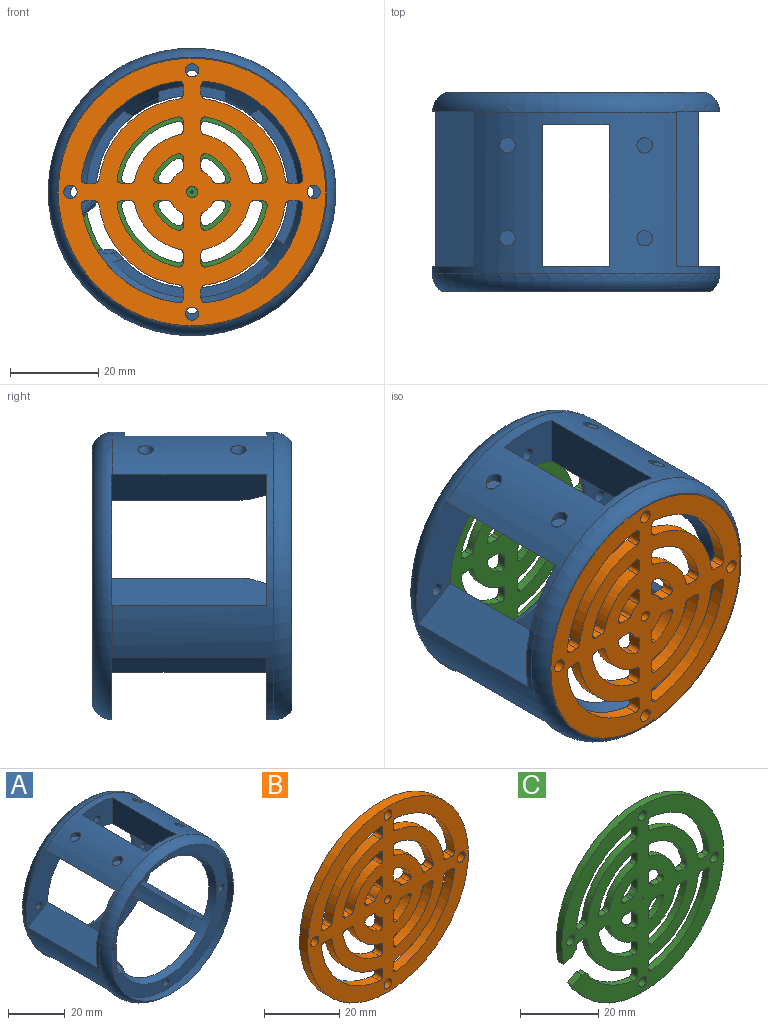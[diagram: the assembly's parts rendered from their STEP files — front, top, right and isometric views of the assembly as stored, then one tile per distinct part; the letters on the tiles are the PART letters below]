
ASSEMBLY  parts=3 mates=1
PART A: 57 faces, bbox 70.6x46.6x70.6 mm
  f0: torus R=28.75mm, axis (0,-1,0), area 6.5mm2, adj f9,f21,f33,f54
  f1: torus R=28.75mm, axis (0,-1,0), area 15.9mm2, adj f9,f21,f50,f55
  f2: cylinder r=1.5mm len=3mm, axis (0,1,0), area 22.1mm2, adj f13,f49
  f3: cylinder r=1.5mm len=3mm, axis (0,1,0), area 22.1mm2, adj f13,f53
  f4: cylinder r=1.5mm len=3mm, axis (0,1,0), area 22.1mm2, adj f13,f45
  f5: torus R=28.75mm, axis (0,-1,0), area 23mm2, adj f9,f21,f43,f47
  f6: cylinder r=1.5mm len=3mm, axis (0,-1,0), area 25mm2, adj f8,f42
  f7: torus R=28.75mm, axis (0,-1,0), area 21.7mm2, adj f9,f21,f44,f51
  f8: plane 61.12x61.12mm, normal (0,-1,0), area 883mm2, adj f6,f11,f16,f17,f18,f20,f21,f32
  f9: cylinder r=21.75mm len=43.5mm, axis (0,1,0), area 709.7mm2, adj f0,f1,f5,f7,f30,f34,f36,f38
  f10: cylinder r=32.5mm len=65mm, axis (0,1,0), area 2231.8mm2, adj f14,f15,f22,f24,f26,f28,f41,f42
  f11: cylinder r=30.5mm len=61mm, axis (0,-1,0), area 574.9mm2, adj f8,f15
  f12: cylinder r=29.5mm len=59mm, axis (0,1,0), area 370.7mm2, adj f13,f14
  f13: plane 59x59mm, normal (0,1,0), area 879.8mm2, adj f2,f3,f4,f12,f19,f31,f36
  f14: torus R=27.5mm, axis (0,1,0), area 1114mm2, adj f10,f12,f45,f47,f48,f49,f50,f51
  f15: torus R=27.5mm, axis (0,-1,0), area 926.8mm2, adj f10,f11
  f16: cylinder r=1.5mm len=3mm, axis (0,-1,0), area 25mm2, adj f8,f56
  f17: cylinder r=1.5mm len=3mm, axis (0,-1,0), area 25mm2, adj f8,f46
  f18: cylinder r=1.5mm len=3mm, axis (0,-1,0), area 25mm2, adj f8,f52
  f19: cylinder r=1.5mm len=5.35mm, axis (0,1,0), area 50.4mm2, adj f13,f41
  f20: cylinder r=5mm len=38mm, axis (0,1,0), area 517.1mm2, adj f8,f31,f32,f33,f34,f38,f39,f40
  f21: cone r=25.25mm half-angle=26.6deg, axis (0,-1,0), area 507.2mm2, adj f0,f1,f5,f7,f8,f30,f32,f40
  f22: cylinder r=1.75mm len=3.5mm, axis (0,0,1), area 11.3mm2, adj f10,f23
  f23: plane 3.5x3.5mm, normal (0,0,1), area 9.6mm2, adj f22
  f24: cylinder r=1.75mm len=3.5mm, axis (0,0,1), area 11.3mm2, adj f10,f25
  f25: plane 3.5x3.5mm, normal (0,0,1), area 9.6mm2, adj f24
  f26: cylinder r=1.75mm len=3.5mm, axis (0,0,1), area 11.3mm2, adj f10,f27
  f27: plane 3.5x3.5mm, normal (0,0,1), area 9.6mm2, adj f26
  f28: cylinder r=1.75mm len=3.5mm, axis (0,0,1), area 11.3mm2, adj f10,f29
  f29: plane 3.5x3.5mm, normal (0,0,1), area 9.6mm2, adj f28
  f30: torus R=28.75mm, axis (0,-1,0), area 4.3mm2, adj f9,f21,f39,f48
  f31: torus R=7mm, axis (0,1,0), area 51.5mm2, adj f13,f20,f35,f37
  f32: bspline ~10.87x6.72mm, area 12.7mm2, adj f8,f20,f21,f33
  f33: bspline ~5.68x2.87mm, area 6.4mm2, adj f0,f20,f32,f34
  f34: cylinder r=2mm len=29.35mm, axis (0,1,0), area 66.7mm2, adj f9,f20,f33,f35
  f35: sphere r=2mm, area 4.9mm2, adj f31,f34,f36
  f36: torus R=23.75mm, axis (0,1,0), area 401.8mm2, adj f9,f13,f35,f37
  f37: sphere r=2mm, area 4.9mm2, adj f31,f36,f38
  f38: cylinder r=2mm len=29.35mm, axis (0,1,0), area 66.7mm2, adj f9,f20,f37,f39
  f39: bspline ~5.68x2.38mm, area 6.4mm2, adj f20,f30,f38,f40
  f40: bspline ~10.87x5.31mm, area 12.7mm2, adj f8,f20,f21,f39
  f41: plane 15x12.08mm, normal (0,-1,0), area 156.4mm2, adj f9,f10,f19,f43,f44
  f42: plane 15x9.78mm, normal (0,1,0), area 123.2mm2, adj f6,f10,f21,f43,f44
  f43: plane 32.13x11.34mm, normal (1,0,0), area 353.4mm2, adj f5,f9,f10,f21,f41,f42
  f44: plane 32.13x11.34mm, normal (-1,0,0), area 353.4mm2, adj f7,f9,f10,f21,f41,f42
  f45: plane 29.47x19.13mm, normal (0,-1,0), area 273.9mm2, adj f4,f9,f14,f47,f48
  f46: plane 29.48x17.13mm, normal (0,1,0), area 227.4mm2, adj f10,f17,f21,f47,f48
  f47: plane 35.14x9.85mm, normal (-0.51,0,-0.86), area 389.3mm2, adj f5,f9,f10,f14,f21,f45,f46
  f48: plane 35.2x10.28mm, normal (-0.52,0,0.85), area 407.3mm2, adj f9,f10,f14,f21,f30,f45,f46
  f49: plane 40.21x19.44mm, normal (0,-1,0), area 395.8mm2, adj f2,f9,f14,f50,f51
  f50: plane 35.04x8.8mm, normal (0.58,0,0.81), area 372.9mm2, adj f1,f9,f10,f14,f21,f49,f52
  f51: plane 35.14x9.76mm, normal (0.52,0,-0.85), area 389.5mm2, adj f7,f9,f10,f14,f21,f49,f52
  f52: plane 40.22x17.46mm, normal (0,1,0), area 325.4mm2, adj f10,f18,f21,f50,f51
  f53: plane 50.92x17.92mm, normal (0,-1,0), area 499.6mm2, adj f3,f9,f14,f54,f55
  f54: plane 35.18x11.39mm, normal (0.28,0,-0.96), area 402.7mm2, adj f0,f9,f10,f14,f21,f53,f56
  f55: plane 35.01x8mm, normal (-0.67,0,-0.74), area 371.3mm2, adj f1,f9,f10,f14,f21,f53,f56
  f56: plane 50.93x16.66mm, normal (0,1,0), area 417.4mm2, adj f10,f16,f21,f54,f55
PART B: 104 faces, bbox 60.5x3x60.5 mm
  f0: plane 3x2.2mm, normal (0,0,-1), area 6.6mm2, adj f50,f51,f93,f102
  f1: cylinder r=9.25mm len=5.25mm, axis (0,1,0), area 22.9mm2, adj f50,f51,f93,f94
  f2: plane 3x2.2mm, normal (1,0,0), area 6.6mm2, adj f50,f51,f94,f103
  f3: cylinder r=9.25mm len=5.25mm, axis (0,1,0), area 22.9mm2, adj f50,f51,f90,f91
  f4: plane 3x2.2mm, normal (0,0,-1), area 6.6mm2, adj f50,f51,f91,f100
  f5: cylinder r=5.25mm len=3mm, axis (0,1,0), area 9mm2, adj f50,f51,f100,f101
  f6: plane 3x2.04mm, normal (0,0,-1), area 6.1mm2, adj f50,f51,f85,f92
  f7: cylinder r=17.25mm len=13.77mm, axis (0,1,0), area 62.1mm2, adj f50,f51,f85,f87
  f8: plane 3x2.04mm, normal (1,0,0), area 6.1mm2, adj f50,f51,f87,f95
  f9: cylinder r=9.25mm len=5.25mm, axis (0,1,0), area 22.9mm2, adj f50,f51,f78,f81
  f10: plane 3x2.2mm, normal (-1,0,0), area 6.6mm2, adj f50,f51,f78,f98
  f11: cylinder r=5.25mm len=3mm, axis (0,1,0), area 9mm2, adj f50,f51,f98,f99
  f12: plane 3x2.2mm, normal (1,0,0), area 6.6mm2, adj f50,f51,f79,f97
  f13: cylinder r=9.25mm len=5.25mm, axis (0,1,0), area 22.9mm2, adj f50,f51,f79,f82
  f14: plane 3x2.2mm, normal (0,0,1), area 6.6mm2, adj f50,f51,f82,f96
  f15: plane 3x2.04mm, normal (-1,0,0), area 6.1mm2, adj f50,f51,f72,f89
  f16: cylinder r=17.25mm len=13.77mm, axis (0,1,0), area 62.1mm2, adj f50,f51,f72,f73
  f17: plane 3x2.04mm, normal (0,0,-1), area 6.1mm2, adj f50,f51,f73,f88
  f18: cylinder r=17.25mm len=13.77mm, axis (0,1,0), area 62.1mm2, adj f50,f51,f70,f71
  f19: plane 3x2.04mm, normal (0,0,1), area 6.1mm2, adj f50,f51,f71,f83
  f20: cylinder r=13.25mm len=10.16mm, axis (0,1,0), area 45.6mm2, adj f50,f51,f76,f83
  f21: plane 3x2.04mm, normal (0,0,1), area 6.1mm2, adj f50,f51,f65,f80
  f22: cylinder r=17.25mm len=13.77mm, axis (0,1,0), area 62.1mm2, adj f50,f51,f65,f66
  f23: plane 3x2.04mm, normal (-1,0,0), area 6.1mm2, adj f50,f51,f66,f77
  f24: plane 3x2.02mm, normal (-1,0,0), area 6.1mm2, adj f50,f51,f62,f75
  f25: cylinder r=25.25mm len=21.93mm, axis (0,1,0), area 100.2mm2, adj f50,f51,f62,f63
  f26: plane 3x2.02mm, normal (0,0,-1), area 6.1mm2, adj f50,f51,f63,f74
  f27: plane 3x2.02mm, normal (0,0,-1), area 6.1mm2, adj f50,f51,f60,f84
  f28: cylinder r=25.25mm len=21.93mm, axis (0,1,0), area 100.2mm2, adj f50,f51,f60,f61
  f29: plane 3x2.02mm, normal (1,0,0), area 6.1mm2, adj f50,f51,f61,f86
  f30: plane 3x2.02mm, normal (1,0,0), area 6.1mm2, adj f50,f51,f58,f69
  f31: cylinder r=25.25mm len=21.93mm, axis (0,1,0), area 100.2mm2, adj f50,f51,f58,f59
  f32: plane 3x2.02mm, normal (0,0,1), area 6.1mm2, adj f50,f51,f59,f68
  f33: cylinder r=25.25mm len=21.93mm, axis (0,1,0), area 100.2mm2, adj f50,f51,f56,f57
  f34: plane 3x2.02mm, normal (-1,0,0), area 6.1mm2, adj f50,f51,f57,f67
  f35: cylinder r=21.25mm len=18.19mm, axis (0,1,0), area 82.9mm2, adj f50,f51,f64,f67
  f36: cylinder r=5.25mm len=3mm, axis (0,1,0), area 9mm2, adj f50,f51,f102,f103
  f37: plane 3x2.2mm, normal (-1,0,0), area 6.6mm2, adj f50,f51,f90,f101
  f38: cylinder r=13.25mm len=10.16mm, axis (0,1,0), area 45.6mm2, adj f50,f51,f92,f95
  f39: plane 3x2.2mm, normal (0,0,1), area 6.6mm2, adj f50,f51,f81,f99
  f40: cylinder r=5.25mm len=3mm, axis (0,1,0), area 9mm2, adj f50,f51,f96,f97
  f41: cylinder r=13.25mm len=10.16mm, axis (0,1,0), area 45.6mm2, adj f50,f51,f88,f89
  f42: plane 3x2.04mm, normal (1,0,0), area 6.1mm2, adj f50,f51,f70,f76
  f43: cylinder r=13.25mm len=10.16mm, axis (0,1,0), area 45.6mm2, adj f50,f51,f77,f80
  f44: cylinder r=21.25mm len=18.19mm, axis (0,1,0), area 82.9mm2, adj f50,f51,f74,f75
  f45: cylinder r=21.25mm len=18.19mm, axis (0,1,0), area 82.9mm2, adj f50,f51,f84,f86
  f46: cylinder r=21.25mm len=18.19mm, axis (0,1,0), area 82.9mm2, adj f50,f51,f68,f69
  f47: plane 3x2.02mm, normal (0,0,1), area 6.1mm2, adj f50,f51,f56,f64
  f48: cylinder r=30.25mm len=60.5mm, axis (0,1,0), area 570.2mm2, adj f50,f51
  f49: cylinder r=1.25mm len=3mm, axis (0,1,0), area 23.6mm2, adj f50,f51
  f50: plane 60.5x60.5mm, normal (0,-1,0), area 1896mm2, adj f0,f1,f2,f3,f4,f5,f6,f7
  f51: plane 60.5x60.5mm, normal (0,1,0), area 1896mm2, adj f0,f1,f2,f3,f4,f5,f6,f7
  f52: cylinder r=1.5mm len=3mm, axis (0,-1,0), area 28.3mm2, adj f50,f51
  f53: cylinder r=1.5mm len=3mm, axis (0,-1,0), area 28.3mm2, adj f50,f51
  f54: cylinder r=1.5mm len=3mm, axis (0,-1,0), area 28.3mm2, adj f50,f51
  f55: cylinder r=1.5mm len=3mm, axis (0,-1,0), area 28.3mm2, adj f50,f51
  f56: cylinder r=1mm len=3mm, axis (0,1,0), area 5.1mm2, adj f33,f47,f50,f51
  f57: cylinder r=1mm len=3mm, axis (0,1,0), area 5.1mm2, adj f33,f34,f50,f51
  f58: cylinder r=1mm len=3mm, axis (0,1,0), area 5.1mm2, adj f30,f31,f50,f51
  f59: cylinder r=1mm len=3mm, axis (0,1,0), area 5.1mm2, adj f31,f32,f50,f51
  f60: cylinder r=1mm len=3mm, axis (0,1,0), area 5.1mm2, adj f27,f28,f50,f51
  f61: cylinder r=1mm len=3mm, axis (0,1,0), area 5.1mm2, adj f28,f29,f50,f51
  f62: cylinder r=1mm len=3mm, axis (0,1,0), area 5.1mm2, adj f24,f25,f50,f51
  f63: cylinder r=1mm len=3mm, axis (0,1,0), area 5.1mm2, adj f25,f26,f50,f51
  f64: cylinder r=1mm len=3mm, axis (0,1,0), area 4.3mm2, adj f35,f47,f50,f51
  f65: cylinder r=1mm len=3mm, axis (0,1,0), area 5.3mm2, adj f21,f22,f50,f51
  f66: cylinder r=1mm len=3mm, axis (0,1,0), area 5.3mm2, adj f22,f23,f50,f51
  f67: cylinder r=1mm len=3mm, axis (0,1,0), area 4.3mm2, adj f34,f35,f50,f51
  f68: cylinder r=1mm len=3mm, axis (0,1,0), area 4.3mm2, adj f32,f46,f50,f51
  f69: cylinder r=1mm len=3mm, axis (0,1,0), area 4.3mm2, adj f30,f46,f50,f51
  f70: cylinder r=1mm len=3mm, axis (0,1,0), area 5.3mm2, adj f18,f42,f50,f51
  f71: cylinder r=1mm len=3mm, axis (0,1,0), area 5.3mm2, adj f18,f19,f50,f51
  f72: cylinder r=1mm len=3mm, axis (0,1,0), area 5.3mm2, adj f15,f16,f50,f51
  f73: cylinder r=1mm len=3mm, axis (0,1,0), area 5.3mm2, adj f16,f17,f50,f51
  f74: cylinder r=1mm len=3mm, axis (0,1,0), area 4.3mm2, adj f26,f44,f50,f51
  f75: cylinder r=1mm len=3mm, axis (0,1,0), area 4.3mm2, adj f24,f44,f50,f51
  f76: cylinder r=1mm len=3mm, axis (0,1,0), area 4.1mm2, adj f20,f42,f50,f51
  f77: cylinder r=1mm len=3mm, axis (0,1,0), area 4.1mm2, adj f23,f43,f50,f51
  f78: cylinder r=1mm len=3mm, axis (0,1,0), area 5.8mm2, adj f9,f10,f50,f51
  f79: cylinder r=1mm len=3mm, axis (0,1,0), area 5.8mm2, adj f12,f13,f50,f51
  f80: cylinder r=1mm len=3mm, axis (0,1,0), area 4.1mm2, adj f21,f43,f50,f51
  f81: cylinder r=1mm len=3mm, axis (0,1,0), area 5.8mm2, adj f9,f39,f50,f51
  f82: cylinder r=1mm len=3mm, axis (0,1,0), area 5.8mm2, adj f13,f14,f50,f51
  f83: cylinder r=1mm len=3mm, axis (0,1,0), area 4.1mm2, adj f19,f20,f50,f51
  f84: cylinder r=1mm len=3mm, axis (0,1,0), area 4.3mm2, adj f27,f45,f50,f51
  f85: cylinder r=1mm len=3mm, axis (0,1,0), area 5.3mm2, adj f6,f7,f50,f51
  f86: cylinder r=1mm len=3mm, axis (0,1,0), area 4.3mm2, adj f29,f45,f50,f51
  f87: cylinder r=1mm len=3mm, axis (0,1,0), area 5.3mm2, adj f7,f8,f50,f51
  f88: cylinder r=1mm len=3mm, axis (0,1,0), area 4.1mm2, adj f17,f41,f50,f51
  f89: cylinder r=1mm len=3mm, axis (0,1,0), area 4.1mm2, adj f15,f41,f50,f51
  f90: cylinder r=1mm len=3mm, axis (0,1,0), area 5.8mm2, adj f3,f37,f50,f51
  f91: cylinder r=1mm len=3mm, axis (0,1,0), area 5.8mm2, adj f3,f4,f50,f51
  f92: cylinder r=1mm len=3mm, axis (0,1,0), area 4.1mm2, adj f6,f38,f50,f51
  f93: cylinder r=1mm len=3mm, axis (0,1,0), area 5.8mm2, adj f0,f1,f50,f51
  f94: cylinder r=1mm len=3mm, axis (0,1,0), area 5.8mm2, adj f1,f2,f50,f51
  f95: cylinder r=1mm len=3mm, axis (0,1,0), area 4.1mm2, adj f8,f38,f50,f51
  f96: cylinder r=1mm len=3mm, axis (0,1,0), area 3.2mm2, adj f14,f40,f50,f51
  f97: cylinder r=1mm len=3mm, axis (0,1,0), area 3.2mm2, adj f12,f40,f50,f51
  f98: cylinder r=1mm len=3mm, axis (0,1,0), area 3.2mm2, adj f10,f11,f50,f51
  f99: cylinder r=1mm len=3mm, axis (0,1,0), area 3.2mm2, adj f11,f39,f50,f51
  f100: cylinder r=1mm len=3mm, axis (0,1,0), area 3.2mm2, adj f4,f5,f50,f51
  f101: cylinder r=1mm len=3mm, axis (0,1,0), area 3.2mm2, adj f5,f37,f50,f51
  f102: cylinder r=1mm len=3mm, axis (0,1,0), area 3.2mm2, adj f0,f36,f50,f51
  f103: cylinder r=1mm len=3mm, axis (0,1,0), area 3.2mm2, adj f2,f36,f50,f51
PART C: 109 faces, bbox 58.5x2x58.5 mm
  f0: plane 58.5x58.5mm, normal (0,-1,0), area 1746.5mm2, adj f2,f3,f4,f5,f6,f7,f8,f9
  f1: plane 58.5x58.5mm, normal (0,1,0), area 1746.5mm2, adj f2,f3,f4,f5,f6,f7,f8,f9
  f2: cylinder r=24.25mm len=2mm, axis (0,1,0), area 1.6mm2, adj f0,f1,f62,f107
  f3: cylinder r=24.25mm len=17.39mm, axis (0,1,0), area 42.6mm2, adj f0,f1,f64,f108
  f4: cylinder r=8.25mm len=4.1mm, axis (0,1,0), area 11.8mm2, adj f0,f1,f94,f97
  f5: plane 2.29x2mm, normal (0,0,1), area 4.6mm2, adj f0,f1,f94,f103
  f6: cylinder r=4.25mm len=2mm, axis (0,1,0), area 3mm2, adj f0,f1,f102,f103
  f7: plane 2.05x2mm, normal (1,0,0), area 4.1mm2, adj f0,f1,f86,f96
  f8: cylinder r=16.25mm len=12.74mm, axis (0,1,0), area 38.2mm2, adj f0,f1,f86,f89
  f9: plane 2.05x2mm, normal (0,0,1), area 4.1mm2, adj f0,f1,f89,f95
  f10: plane 2.29x2mm, normal (0,0,1), area 4.6mm2, adj f0,f1,f84,f100
  f11: cylinder r=8.25mm len=4.1mm, axis (0,1,0), area 11.8mm2, adj f0,f1,f84,f99
  f12: plane 2.29x2mm, normal (-1,0,0), area 4.6mm2, adj f0,f1,f99,f101
  f13: plane 2.05x2mm, normal (0,0,1), area 4.1mm2, adj f0,f1,f78,f81
  f14: cylinder r=16.25mm len=12.74mm, axis (0,1,0), area 38.2mm2, adj f0,f1,f78,f79
  f15: plane 2.05x2mm, normal (-1,0,0), area 4.1mm2, adj f0,f1,f79,f98
  f16: plane 2.29x2mm, normal (-1,0,0), area 4.6mm2, adj f0,f1,f71,f73
  f17: cylinder r=8.25mm len=4.1mm, axis (0,1,0), area 11.8mm2, adj f0,f1,f71,f83
  f18: plane 2.29x2mm, normal (0,0,-1), area 4.6mm2, adj f0,f1,f83,f85
  f19: cylinder r=8.25mm len=4.1mm, axis (0,1,0), area 11.8mm2, adj f0,f1,f72,f93
  f20: plane 2.29x2mm, normal (1,0,0), area 4.6mm2, adj f0,f1,f72,f74
  f21: cylinder r=4.25mm len=2mm, axis (0,1,0), area 3mm2, adj f0,f1,f74,f104
  f22: plane 2.05x2mm, normal (-1,0,0), area 4.1mm2, adj f0,f1,f67,f69
  f23: cylinder r=16.25mm len=12.74mm, axis (0,1,0), area 38.2mm2, adj f0,f1,f67,f77
  f24: plane 2.05x2mm, normal (0,0,-1), area 4.1mm2, adj f0,f1,f77,f82
  f25: cylinder r=16.25mm len=12.74mm, axis (0,1,0), area 38.2mm2, adj f0,f1,f68,f91
  f26: plane 2.05x2mm, normal (1,0,0), area 4.1mm2, adj f0,f1,f68,f70
  f27: cylinder r=12.25mm len=9.16mm, axis (0,1,0), area 27.3mm2, adj f0,f1,f70,f92
  f28: plane 2.02x2mm, normal (0,0,-1), area 4mm2, adj f0,f1,f62,f75
  f29: cylinder r=20.25mm len=17.19mm, axis (0,1,0), area 52.1mm2, adj f0,f1,f66,f75
  f30: plane 2.02x2mm, normal (0,0,-1), area 4mm2, adj f0,f1,f61,f90
  f31: cylinder r=24.25mm len=20.92mm, axis (0,1,0), area 63.6mm2, adj f0,f1,f61,f63
  f32: plane 2.02x2mm, normal (1,0,0), area 4mm2, adj f0,f1,f63,f65
  f33: plane 2.02x2mm, normal (1,0,0), area 4mm2, adj f0,f1,f59,f87
  f34: cylinder r=24.25mm len=20.92mm, axis (0,1,0), area 63.6mm2, adj f0,f1,f59,f60
  f35: plane 2.02x2mm, normal (0,0,1), area 4mm2, adj f0,f1,f60,f88
  f36: cylinder r=24.25mm len=20.92mm, axis (0,1,0), area 63.6mm2, adj f0,f1,f57,f58
  f37: plane 2.02x2mm, normal (-1,0,0), area 4mm2, adj f0,f1,f58,f80
  f38: cylinder r=20.25mm len=17.19mm, axis (0,1,0), area 52.1mm2, adj f0,f1,f76,f80
  f39: plane 2.29x2mm, normal (1,0,0), area 4.6mm2, adj f0,f1,f97,f102
  f40: cylinder r=12.25mm len=9.16mm, axis (0,1,0), area 27.3mm2, adj f0,f1,f95,f96
  f41: cylinder r=4.25mm len=2mm, axis (0,1,0), area 3mm2, adj f0,f1,f100,f101
  f42: cylinder r=12.25mm len=9.16mm, axis (0,1,0), area 27.3mm2, adj f0,f1,f81,f98
  f43: cylinder r=4.25mm len=2mm, axis (0,1,0), area 3mm2, adj f0,f1,f73,f85
  f44: plane 2.29x2mm, normal (0,0,-1), area 4.6mm2, adj f0,f1,f93,f104
  f45: cylinder r=12.25mm len=9.16mm, axis (0,1,0), area 27.3mm2, adj f0,f1,f69,f82
  f46: plane 2.05x2mm, normal (0,0,-1), area 4.1mm2, adj f0,f1,f91,f92
  f47: plane 2.02x2mm, normal (-1,0,0), area 4mm2, adj f0,f1,f64,f66
  f48: cylinder r=20.25mm len=17.19mm, axis (0,1,0), area 52.1mm2, adj f0,f1,f65,f90
  f49: cylinder r=20.25mm len=17.19mm, axis (0,1,0), area 52.1mm2, adj f0,f1,f87,f88
  f50: plane 2.02x2mm, normal (0,0,1), area 4mm2, adj f0,f1,f57,f76
  f51: cylinder r=29.25mm len=58.5mm, axis (0,1,0), area 349.8mm2, adj f0,f1,f105,f106
  f52: cylinder r=0.25mm len=2mm, axis (0,1,0), area 3.1mm2, adj f0,f1
  f53: cylinder r=1.5mm len=3mm, axis (0,-1,0), area 18.8mm2, adj f0,f1
  f54: cylinder r=1.5mm len=3mm, axis (0,-1,0), area 18.8mm2, adj f0,f1
  f55: cylinder r=1.5mm len=3mm, axis (0,-1,0), area 18.8mm2, adj f0,f1
  f56: cylinder r=1.5mm len=3mm, axis (0,-1,0), area 18.8mm2, adj f0,f1
  f57: cylinder r=1mm len=2mm, axis (0,1,0), area 3.4mm2, adj f0,f1,f36,f50
  f58: cylinder r=1mm len=2mm, axis (0,1,0), area 3.4mm2, adj f0,f1,f36,f37
  f59: cylinder r=1mm len=2mm, axis (0,1,0), area 3.4mm2, adj f0,f1,f33,f34
  f60: cylinder r=1mm len=2mm, axis (0,1,0), area 3.4mm2, adj f0,f1,f34,f35
  f61: cylinder r=1mm len=2mm, axis (0,1,0), area 3.4mm2, adj f0,f1,f30,f31
  f62: cylinder r=1mm len=2mm, axis (0,1,0), area 3.4mm2, adj f0,f1,f2,f28
  f63: cylinder r=1mm len=2mm, axis (0,1,0), area 3.4mm2, adj f0,f1,f31,f32
  f64: cylinder r=1mm len=2mm, axis (0,1,0), area 3.4mm2, adj f0,f1,f3,f47
  f65: cylinder r=1mm len=2mm, axis (0,1,0), area 2.9mm2, adj f0,f1,f32,f48
  f66: cylinder r=1mm len=2mm, axis (0,1,0), area 2.9mm2, adj f0,f1,f29,f47
  f67: cylinder r=1mm len=2mm, axis (0,1,0), area 3.5mm2, adj f0,f1,f22,f23
  f68: cylinder r=1mm len=2mm, axis (0,1,0), area 3.5mm2, adj f0,f1,f25,f26
  f69: cylinder r=1mm len=2mm, axis (0,1,0), area 2.7mm2, adj f0,f1,f22,f45
  f70: cylinder r=1mm len=2mm, axis (0,1,0), area 2.7mm2, adj f0,f1,f26,f27
  f71: cylinder r=1mm len=2mm, axis (0,1,0), area 4mm2, adj f0,f1,f16,f17
  f72: cylinder r=1mm len=2mm, axis (0,1,0), area 4mm2, adj f0,f1,f19,f20
  f73: cylinder r=1mm len=2mm, axis (0,1,0), area 1.9mm2, adj f0,f1,f16,f43
  f74: cylinder r=1mm len=2mm, axis (0,1,0), area 1.9mm2, adj f0,f1,f20,f21
  f75: cylinder r=1mm len=2mm, axis (0,1,0), area 2.9mm2, adj f0,f1,f28,f29
  f76: cylinder r=1mm len=2mm, axis (0,1,0), area 2.9mm2, adj f0,f1,f38,f50
  f77: cylinder r=1mm len=2mm, axis (0,1,0), area 3.5mm2, adj f0,f1,f23,f24
  f78: cylinder r=1mm len=2mm, axis (0,1,0), area 3.5mm2, adj f0,f1,f13,f14
  f79: cylinder r=1mm len=2mm, axis (0,1,0), area 3.5mm2, adj f0,f1,f14,f15
  f80: cylinder r=1mm len=2mm, axis (0,1,0), area 2.9mm2, adj f0,f1,f37,f38
  f81: cylinder r=1mm len=2mm, axis (0,1,0), area 2.7mm2, adj f0,f1,f13,f42
  f82: cylinder r=1mm len=2mm, axis (0,1,0), area 2.7mm2, adj f0,f1,f24,f45
  f83: cylinder r=1mm len=2mm, axis (0,1,0), area 4mm2, adj f0,f1,f17,f18
  f84: cylinder r=1mm len=2mm, axis (0,1,0), area 4mm2, adj f0,f1,f10,f11
  f85: cylinder r=1mm len=2mm, axis (0,1,0), area 1.9mm2, adj f0,f1,f18,f43
  f86: cylinder r=1mm len=2mm, axis (0,1,0), area 3.5mm2, adj f0,f1,f7,f8
  f87: cylinder r=1mm len=2mm, axis (0,1,0), area 2.9mm2, adj f0,f1,f33,f49
  f88: cylinder r=1mm len=2mm, axis (0,1,0), area 2.9mm2, adj f0,f1,f35,f49
  f89: cylinder r=1mm len=2mm, axis (0,1,0), area 3.5mm2, adj f0,f1,f8,f9
  f90: cylinder r=1mm len=2mm, axis (0,1,0), area 2.9mm2, adj f0,f1,f30,f48
  f91: cylinder r=1mm len=2mm, axis (0,1,0), area 3.5mm2, adj f0,f1,f25,f46
  f92: cylinder r=1mm len=2mm, axis (0,1,0), area 2.7mm2, adj f0,f1,f27,f46
  f93: cylinder r=1mm len=2mm, axis (0,1,0), area 4mm2, adj f0,f1,f19,f44
  f94: cylinder r=1mm len=2mm, axis (0,1,0), area 4mm2, adj f0,f1,f4,f5
  f95: cylinder r=1mm len=2mm, axis (0,1,0), area 2.7mm2, adj f0,f1,f9,f40
  f96: cylinder r=1mm len=2mm, axis (0,1,0), area 2.7mm2, adj f0,f1,f7,f40
  f97: cylinder r=1mm len=2mm, axis (0,1,0), area 4mm2, adj f0,f1,f4,f39
  f98: cylinder r=1mm len=2mm, axis (0,1,0), area 2.7mm2, adj f0,f1,f15,f42
  f99: cylinder r=1mm len=2mm, axis (0,1,0), area 4mm2, adj f0,f1,f11,f12
  f100: cylinder r=1mm len=2mm, axis (0,1,0), area 1.9mm2, adj f0,f1,f10,f41
  f101: cylinder r=1mm len=2mm, axis (0,1,0), area 1.9mm2, adj f0,f1,f12,f41
  f102: cylinder r=1mm len=2mm, axis (0,1,0), area 1.9mm2, adj f0,f1,f6,f39
  f103: cylinder r=1mm len=2mm, axis (0,1,0), area 1.9mm2, adj f0,f1,f5,f6
  f104: cylinder r=1mm len=2mm, axis (0,1,0), area 1.9mm2, adj f0,f1,f21,f44
  f105: plane 3.26x2mm, normal (-0.49,0,0.87), area 7.5mm2, adj f0,f1,f51,f108
  f106: plane 3.28x2mm, normal (0.29,0,-0.96), area 6.9mm2, adj f0,f1,f51,f107
  f107: cylinder r=5mm len=2mm, axis (0,1,0), area 4mm2, adj f0,f1,f2,f106
  f108: cylinder r=5mm len=2mm, axis (0,1,0), area 3.1mm2, adj f0,f1,f3,f105
PLACE A t=(35.18,96.17,42.31)mm
PLACE B t=(35.18,54.17,42.31)mm
PLACE C rot(axis=(1,0,0),180deg) t=(35.18,94.17,42.31)mm
MATE fastened C.f2 <-> A.f12  axis (0,-1,0) through (35.18,94.17,42.31)mm
